FCSTD DOCUMENT  (FreeCAD 0.19R24291 (Git))
Label: MiniItxHddHolder
License: All rights reserved
LicenseURL: http://en.wikipedia.org/wiki/All_rights_reserved
objects: Sketcher::SketchObject×2, PartDesign::Body×1
note: 3 computed .brp shape members not serialized (recipe doc carries the construction recipe); baked Part::Feature solids carry a one-line shape summary decoded from their .brp

FEATURE [Sketcher::SketchObject] Sketch  label="T_side"
  FullyConstrained = false
  MapMode = 5
  Placement = pos=(0,0,0) rot=(1,0,0;1.5708rad)
  Support = -> [XZ_Plane]
  sketch-geometry (13):
    g0: LineSegment StartX=1.90898 StartY=-0.05824 StartZ=0 EndX=101.909 EndY=-0.05824 EndZ=0
    g1: LineSegment StartX=101.909 StartY=-0.05824 StartZ=0 EndX=101.909 EndY=-18.0582 EndZ=0
    g2: LineSegment StartX=101.909 StartY=-18.0582 StartZ=0 EndX=1.90898 EndY=-18.0582 EndZ=0
    g3: LineSegment StartX=1.90898 StartY=-18.0582 StartZ=0 EndX=1.90898 EndY=-0.05824 EndZ=0
    g4: LineSegment StartX=1.90898 StartY=-10.0582 StartZ=0 EndX=101.909 EndY=-10.0582 EndZ=0
    g5: Circle CenterX=13.059 CenterY=-6.35824 CenterZ=0 NormalX=0 NormalY=0 NormalZ=1 AngleXU=0 Radius=1.75
    g6: Circle CenterX=89.209 CenterY=-6.35824 CenterZ=0 NormalX=0 NormalY=0 NormalZ=1 AngleXU=0 Radius=1.75
    g7: LineSegment StartX=13.059 StartY=-6.35824 StartZ=0 EndX=89.209 EndY=-6.35824 EndZ=0
    g8: LineSegment StartX=13.059 StartY=-6.35824 StartZ=0 EndX=13.059 EndY=-14.5582 EndZ=0
    g9: LineSegment StartX=13.059 StartY=-14.5582 StartZ=0 EndX=89.209 EndY=-14.5582 EndZ=0
    g10: LineSegment StartX=89.209 StartY=-14.5582 StartZ=0 EndX=89.209 EndY=-6.35824 EndZ=0
    g11: Circle CenterX=13.059 CenterY=-14.5582 CenterZ=0 NormalX=0 NormalY=0 NormalZ=1 AngleXU=0 Radius=1.75
    g12: Circle CenterX=89.209 CenterY=-14.5582 CenterZ=0 NormalX=0 NormalY=0 NormalZ=1 AngleXU=0 Radius=1.75
  constraints (35):
    c: Coincident(g0,g1)
    c: Coincident(g1,g2)
    c: Coincident(g2,g3)
    c: Coincident(g3,g0)
    c: Horizontal(g0)
    c: Horizontal(g2)
    c: Vertical(g1)
    c: Vertical(g3)
    c: DistanceX(g0,g0) = 100
    c: PointOnObject(g4,g1)
    c: DistanceY(g4,g0) = 10
    c: Horizontal(g4)
    c: Radius(g5) = 1.75
    c: Equal(g5,g6)
    c: Coincident(g7,g5)
    c: Coincident(g7,g6)
    c: Horizontal(g7)
    c: DistanceX(g7,g7) = 76.15
    c: DistanceX(g6,g0) = 12.7
    c: DistanceY(g6,g0) = 6.3
    c: DistanceY(g2,g4) = 8
    c: Coincident(g8,g5)
    c: Vertical(g8)
    c: Coincident(g8,g9)
    c: Horizontal(g9)
    c: Coincident(g9,g10)
    c: Coincident(g10,g6)
    c: Vertical(g10)
    c: DistanceY(g9,g4) = 4.5
    c: Coincident(g11,g8)
    c: Coincident(g12,g9)
    c: Equal(g6,g12)
    c: Equal(g12,g11)
    c: PointOnObject(g4,g3)
    c: DistanceY(g1,g1) = 18  'SideHeight'
FEATURE [Sketcher::SketchObject] Sketch001
  ExternalGeometry = -> [Sketch]
  FullyConstrained = true
  MapMode = 5
  Support = -> [XY_Plane]
  sketch-geometry (20):
    g0: LineSegment StartX=1.90898 StartY=-2e-15 StartZ=0 EndX=101.909 EndY=-2e-15 EndZ=0
    g1: LineSegment StartX=101.909 StartY=-2e-15 StartZ=0 EndX=101.909 EndY=70 EndZ=0
    g2: LineSegment StartX=101.909 StartY=70 StartZ=0 EndX=1.90898 EndY=70 EndZ=0
    g3: LineSegment StartX=1.90898 StartY=70 StartZ=0 EndX=1.90898 EndY=0 EndZ=0
    g4: LineSegment StartX=101.909 StartY=-2e-15 StartZ=0 EndX=101.909 EndY=-12 EndZ=0
    g5: LineSegment StartX=101.909 StartY=-12 StartZ=0 EndX=91.909 EndY=-12 EndZ=0
    g6: LineSegment StartX=91.909 StartY=-12 StartZ=0 EndX=91.909 EndY=-1.8e-15 EndZ=0
    g7: Circle CenterX=96.909 CenterY=-6.5 CenterZ=0 NormalX=0 NormalY=0 NormalZ=1 AngleXU=0 Radius=2
    g8: LineSegment StartX=96.909 StartY=-6.5 StartZ=0 EndX=96.909 EndY=-12 EndZ=0
    g9: LineSegment StartX=96.909 StartY=-6.5 StartZ=0 EndX=25.409 EndY=-6.5 EndZ=0
    g10: Circle CenterX=25.409 CenterY=-6.5 CenterZ=0 NormalX=0 NormalY=0 NormalZ=1 AngleXU=0 Radius=2
    g11: LineSegment StartX=20.409 StartY=-2e-15 StartZ=0 EndX=20.409 EndY=-12 EndZ=0
    g12: LineSegment StartX=20.409 StartY=-12 StartZ=0 EndX=30.409 EndY=-12 EndZ=0
    g13: LineSegment StartX=30.409 StartY=-12 StartZ=0 EndX=30.409 EndY=-1.8e-15 EndZ=0
    g14: LineSegment StartX=25.409 StartY=-6.5 StartZ=0 EndX=25.409 EndY=-12 EndZ=0
    g15: Circle CenterX=-3.09102 CenterY=49 CenterZ=0 NormalX=0 NormalY=0 NormalZ=1 AngleXU=0 Radius=2
    g16: LineSegment StartX=-3.09102 StartY=49 StartZ=0 EndX=1.90898 EndY=49 EndZ=0
    g17: LineSegment StartX=1.90898 StartY=55.75 StartZ=0 EndX=-6.39102 EndY=55.75 EndZ=0
    g18: LineSegment StartX=-6.39102 StartY=55.75 StartZ=0 EndX=-6.39102 EndY=42.25 EndZ=0
    g19: LineSegment StartX=-6.39102 StartY=42.25 StartZ=0 EndX=1.90898 EndY=42.25 EndZ=0
  constraints (56):
    c: Coincident(g0,g1)
    c: Coincident(g1,g2)
    c: Coincident(g2,g3)
    c: Coincident(g3,g0)
    c: Horizontal(g2)
    c: Vertical(g1)
    c: Vertical(g3)
    c: Coincident(g0,g-3)
    c: Coincident(g0,g-4)
    c: DistanceY(g3,g3) = 70
    c: Coincident(g0,g4)
    c: Vertical(g4)
    c: Coincident(g4,g5)
    c: Horizontal(g5)
    c: Coincident(g5,g6)
    c: PointOnObject(g6,g0)
    c: Vertical(g6)
    c: DistanceY(g4,g4) = 12
    c: DistanceY(g7,g0) = 6.5
    c: Radius(g7) = 2
    c: Coincident(g8,g7)
    c: Vertical(g8)
    c: Symmetric(g5,g4,g8)
    c: Coincident(g9,g7)
    c: Horizontal(g9)
    c: DistanceX(g9,g9) = 71.5
    c: DistanceX(g6,g0) = 10
    c: Coincident(g10,g9)
    c: Equal(g10,g7)
    c: PointOnObject(g11,g0)
    c: Vertical(g11)
    c: Coincident(g11,g12)
    c: Horizontal(g12)
    c: Coincident(g12,g13)
    c: PointOnObject(g13,g0)
    c: Vertical(g13)
    c: Coincident(g14,g10)
    c: Vertical(g14)
    c: Symmetric(g12,g11,g14)
    c: Equal(g12,g5)
    c: PointOnObject(g5,g12)
    c: Equal(g10,g15)
    c: Coincident(g16,g15)
    c: PointOnObject(g16,g3)
    c: Horizontal(g16)
    c: DistanceY(g15,g2) = 21
    c: PointOnObject(g17,g3)
    c: Horizontal(g17)
    c: Coincident(g17,g18)
    c: Vertical(g18)
    c: Coincident(g18,g19)
    c: Horizontal(g19)
    c: Symmetric(g19,g17,g16)
    c: DistanceY(g18,g18) = 13.5
    c: DistanceX(g17,g17) = 8.3
    c: DistanceX(g15,g19) = 5
FEATURE [PartDesign::Body] Body
  Group = -> [Sketch,Sketch001]
  Origin = -> Origin
